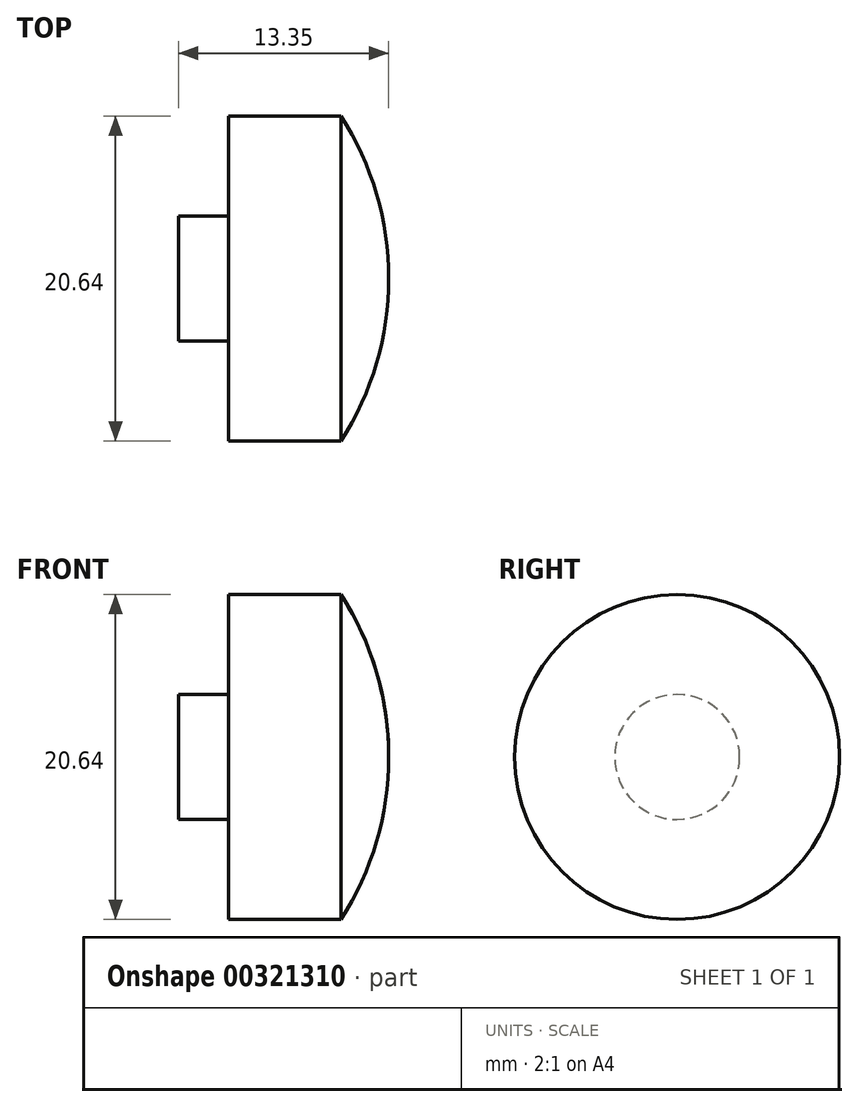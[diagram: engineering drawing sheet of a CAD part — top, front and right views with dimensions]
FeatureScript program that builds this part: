
annotation { "Feature Type Name" : "Feature", "Feature Type Description" : "" }
export const myFeature = defineFeature(function(context is Context, id is Id, definition is map)
    precondition{}
    {
        {
            var Q0;
            Q0=qCreatedBy(makeId("Front.planeOp"),FACE);
            var sketch = newSketch(context, id + "F0", { "sketchPlane" : qUnion([Q0])});
            skLineSegment(sketch, "E0", {"start": v(0, 0) * mm, "end": v(-13.35, 0) * mm});
            skLineSegment(sketch, "E1", {"start": v(-13.35, 0) * mm, "end": v(-13.35, 3.97) * mm});
            skLineSegment(sketch, "E2", {"start": v(-13.35, 3.97) * mm, "end": v(-10.17, 3.97) * mm});
            skLineSegment(sketch, "E3", {"start": v(-10.17, 3.97) * mm, "end": v(-10.17, 10.32) * mm});
            skLineSegment(sketch, "E4", {"start": v(-10.17, 10.32) * mm, "end": v(-3.04, 10.32) * mm});
            skArc(sketch, "E5", {"start": v(0, 0) * mm, "mid": v(-0.77, 5.38) * mm, "end": v(-3.04, 10.32) * mm});
            skLineSegment(sketch, "E6", {"start": v(0, 0) * mm, "end": v(13.3, 0) * mm, "construction": true});
            skSolve(sketch);
        }
        {
            var Q0;
            Q0=makeQuery(id+"F0.imprint","IMPRINT",FACE,{"disambiguationData":[TD([[makeQuery(id+"F0.imprint","IMPRINT",EDGE,{"derivedFrom":sQuery(id+"F0.wireOp",EDGE,"E0")}),-1.0]])]});
            var Q1;
            Q1=sQuery(id+"F0.wireOp",EDGE,"E6");
            revolve(context, id + "F1", {"surfaceOperationType" : NewSurfaceOperationType.NEW, "entities" : qUnion([Q0]), "axis" : qUnion([Q1]), "revolveType" : RevolveType.FULL});
        }
    });
